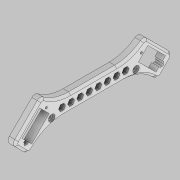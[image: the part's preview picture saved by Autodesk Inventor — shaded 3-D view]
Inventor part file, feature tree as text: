
AUTODESK INVENTOR PART (.ipt)
format: ipt  version: 2022.2 (Build 262287010, 287A)  size: 283,648 bytes
history: native  units: mm
features: extrude x6, sketch x6, fillet x2, other x1, chamfer x1
ambient origin geometry x8: Origin, YZ Plane, XZ Plane, XY Plane, X Axis, Y Axis, Z Axis, Center Point
bodies: Body1 (feature_tree)
feature tree (16):
  other  "Sólido1"
  extrude  "Extrusión1"  Depth=15.0mm
  fillet  "Empalme1"  Radius=20.0mm
  extrude  "Extrusión2"  TaperAngle=0.0deg  [1 undecoded]
  extrude  "Extrusión3"  Depth=3.0mm
  extrude  "Extrusión4"  Depth=7.0mm TaperAngle=0.0deg
  extrude  "Extrusión5"  Depth=5.5mm
  extrude  "Extrusión6"  Depth=2.0mm
  fillet  "Empalme3"  Radius=40.0mm
  chamfer  "Chaflán2"  Distance=7.0mm
  sketch  "Boceto1"  dims[d1=10.0mm d2=15.0mm d4=20.0mm]
  sketch  "Boceto2"  dims[d5=37.0mm d6=0.0mm]
  sketch  "Boceto4"  dims[d7=3.0mm d10=3.8mm]
  sketch  "Boceto5"  dims[d11=39.0mm d14=7.0mm d15=0.0mm]
  sketch  "Boceto6"  dims[d16=40.0mm d17=5.5mm]
  sketch  "Boceto7"  dims[d18=7.5mm d19=4.2mm d20=40.0mm d22=8.4mm d23=10.0mm d25=10.0mm d27=7.0mm d28=0.0mm d32=12.5mm d33=23.0mm d34=10.0mm d35=0.0mm d36=6.0mm d37=6.0mm d38=2.0mm d39=0.0mm d44=4.5mm d45=2.0mm d46=10.0mm d47=0.0mm d48=2.0mm d49=2.0mm d50=27.7mm d51=6.25mm d52=10.0mm d53=0.0mm d62=4.0mm d63=2.0mm d64=2.0mm d65=45.0deg]
note: 1 required parameter value undecoded (feature->parameter linkage not recoverable at this tier; creation-order binding heuristic only, values carry confidence <= 0.55)
